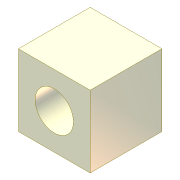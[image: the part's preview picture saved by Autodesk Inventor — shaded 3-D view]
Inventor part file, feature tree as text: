
AUTODESK INVENTOR PART (.ipt)
format: ipt  version: unknown  size: 162,816 bytes
history: native  units: in
note: dims shown in document units (in); Inventor stores cm internally (conversion verified against a paired STEP export)
features: extrude x1, sketch x1
ambient origin geometry x8: Origin, YZ Plane, XZ Plane, XY Plane, X Axis, Y Axis, Z Axis, Center Point
feature tree (2):
  extrude  "Extrusion4"  Depth=1.1811in
  sketch  "Sketch7"  dims[d23=0.6299in d24=1.1811in d25=1.1811in d26=0.0in]
